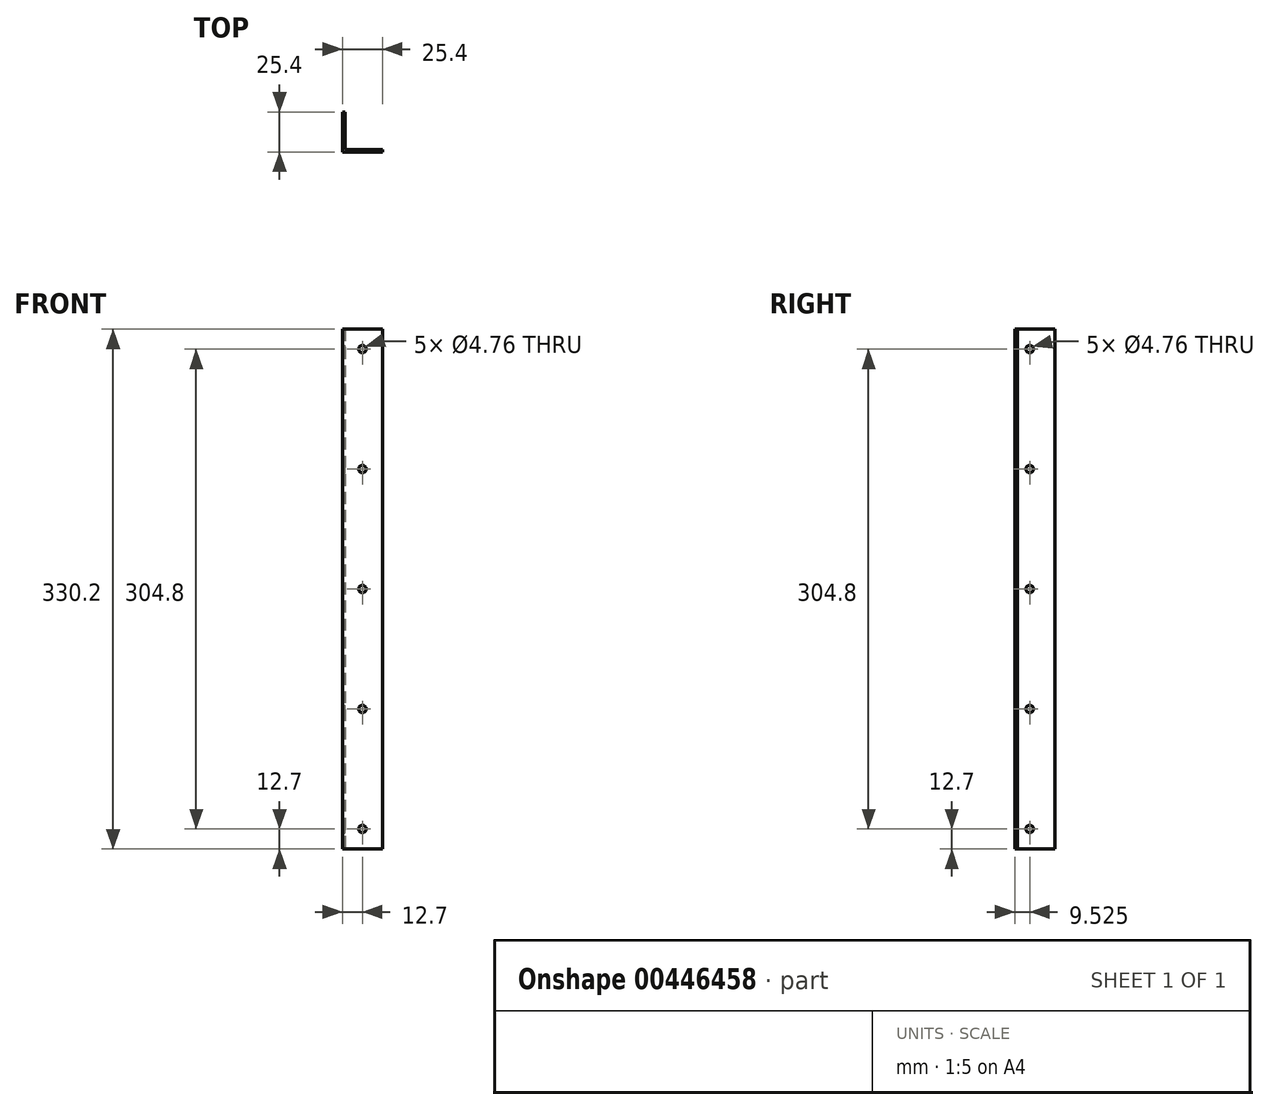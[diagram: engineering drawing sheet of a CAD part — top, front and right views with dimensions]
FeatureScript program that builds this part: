
annotation { "Feature Type Name" : "Feature", "Feature Type Description" : "" }
export const myFeature = defineFeature(function(context is Context, id is Id, definition is map)
    precondition{}
    {
        {
            var Q0;
            Q0=qCreatedBy(makeId("Top.planeOp"),FACE);
            var sketch = newSketch(context, id + "F0", { "sketchPlane" : qUnion([Q0])});
            skLineSegment(sketch, "E0", {"start": v(0, 25.4) * mm, "end": v(0, 0) * mm});
            skLineSegment(sketch, "E1", {"start": v(0, 0) * mm, "end": v(25.4, 0) * mm});
            skLineSegment(sketch, "E2", {"start": v(25.4, 0) * mm, "end": v(25.4, 1.59) * mm});
            skLineSegment(sketch, "E3", {"start": v(25.4, 1.59) * mm, "end": v(1.59, 1.59) * mm});
            skLineSegment(sketch, "E4", {"start": v(1.59, 1.59) * mm, "end": v(1.59, 25.4) * mm});
            skLineSegment(sketch, "E5", {"start": v(1.59, 25.4) * mm, "end": v(0, 25.4) * mm});
            skSolve(sketch);
        }
        {
            var Q0;
            Q0=makeQuery(id+"F0.imprint","IMPRINT",FACE,{"disambiguationData":[TD([[makeQuery(id+"F0.imprint","IMPRINT",EDGE,{"derivedFrom":sQuery(id+"F0.wireOp",EDGE,"E0")}),1.0]])]});
            extrude(context, id + "F1", {"entities" : qUnion([Q0]), "depth" : 330.2 * mm, "offsetDistance" : 25.4 * mm, "symmetric" : true});
        }
        {
            var Q0;
            Q0=makeQuery(id+"F1.opExtrude","SWEPT_FACE",FACE,{"disambiguationData":[OSD([sQuery(id+"F0.wireOp",EDGE,"E3")])]});
            var sketch = newSketch(context, id + "F2", { "sketchPlane" : qUnion([Q0])});
            skCircle(sketch, "E6", {"center": v(-12.7, -152.4) * mm, "radius": 2.38 * mm});
            skCircle(sketch, "E7.0.1.0", {"center": v(-12.7, -76.2) * mm, "radius": 2.38 * mm});
            skCircle(sketch, "E7.0.2.0", {"center": v(-12.7, 0) * mm, "radius": 2.38 * mm});
            skCircle(sketch, "E7.0.3.0", {"center": v(-12.7, 76.2) * mm, "radius": 2.38 * mm});
            skCircle(sketch, "E7.0.4.0", {"center": v(-12.7, 152.4) * mm, "radius": 2.38 * mm});
            skLineSegment(sketch, "E7.direction1", {"start": v(-12.7, -152.4) * mm, "end": v(12.7, -152.4) * mm, "construction": true});
            skLineSegment(sketch, "E7.direction2", {"start": v(-12.7, -152.4) * mm, "end": v(-12.7, -76.2) * mm, "construction": true});
            skSolve(sketch);
        }
        {
            var Q0;
            Q0=makeQuery(id+"F2.imprint","IMPRINT",FACE,{"disambiguationData":[TD([[makeQuery(id+"F2.imprint","IMPRINT",EDGE,{"derivedFrom":sQuery(id+"F2.wireOp",EDGE,"E6")}),1.0]])]});
            var Q1;
            Q1=makeQuery(id+"F2.imprint","IMPRINT",FACE,{"disambiguationData":[TD([[makeQuery(id+"F2.imprint","IMPRINT",EDGE,{"derivedFrom":sQuery(id+"F2.wireOp",EDGE,"E7.0.4.0")}),1.0]])]});
            var Q2;
            Q2=makeQuery(id+"F2.imprint","IMPRINT",FACE,{"disambiguationData":[TD([[makeQuery(id+"F2.imprint","IMPRINT",EDGE,{"derivedFrom":sQuery(id+"F2.wireOp",EDGE,"E7.0.3.0")}),1.0]])]});
            var Q3;
            Q3=makeQuery(id+"F2.imprint","IMPRINT",FACE,{"disambiguationData":[TD([[makeQuery(id+"F2.imprint","IMPRINT",EDGE,{"derivedFrom":sQuery(id+"F2.wireOp",EDGE,"E7.0.1.0")}),1.0]])]});
            var Q4;
            Q4=makeQuery(id+"F2.imprint","IMPRINT",FACE,{"disambiguationData":[TD([[makeQuery(id+"F2.imprint","IMPRINT",EDGE,{"derivedFrom":sQuery(id+"F2.wireOp",EDGE,"E7.0.2.0")}),1.0]])]});
            extrude(context, id + "F3", {"entities" : qUnion([Q0, Q1, Q2, Q3, Q4]), "operationType" : NewBodyOperationType.REMOVE, "endBound" : BoundingType.UP_TO_NEXT, "oppositeDirection" : true, "depth" : 25.4 * mm, "offsetDistance" : 25.4 * mm});
        }
        {
            var Q0;
            Q0=makeQuery(id+"F1.opExtrude","SWEPT_FACE",FACE,{"disambiguationData":[OSD([sQuery(id+"F0.wireOp",EDGE,"E4")])]});
            var sketch = newSketch(context, id + "F4", { "sketchPlane" : qUnion([Q0])});
            skCircle(sketch, "E8", {"center": v(9.52, -152.4) * mm, "radius": 2.38 * mm});
            skCircle(sketch, "E9.0.1.0", {"center": v(9.52, -76.2) * mm, "radius": 2.38 * mm});
            skCircle(sketch, "E9.0.2.0", {"center": v(9.52, 0) * mm, "radius": 2.38 * mm});
            skCircle(sketch, "E9.0.3.0", {"center": v(9.52, 76.2) * mm, "radius": 2.38 * mm});
            skCircle(sketch, "E9.0.4.0", {"center": v(9.52, 152.4) * mm, "radius": 2.38 * mm});
            skLineSegment(sketch, "E9.direction1", {"start": v(9.52, -152.4) * mm, "end": v(46.83, -152.4) * mm, "construction": true});
            skLineSegment(sketch, "E9.direction2", {"start": v(9.52, -152.4) * mm, "end": v(9.52, -76.2) * mm, "construction": true});
            skSolve(sketch);
        }
        {
            var Q0;
            Q0 = qSketchRegion(id + "F4", true);
            extrude(context, id + "F5", {"entities" : qUnion([Q0]), "operationType" : NewBodyOperationType.REMOVE, "oppositeDirection" : true, "depth" : 25.4 * mm, "offsetDistance" : 25.4 * mm});
        }
    });
